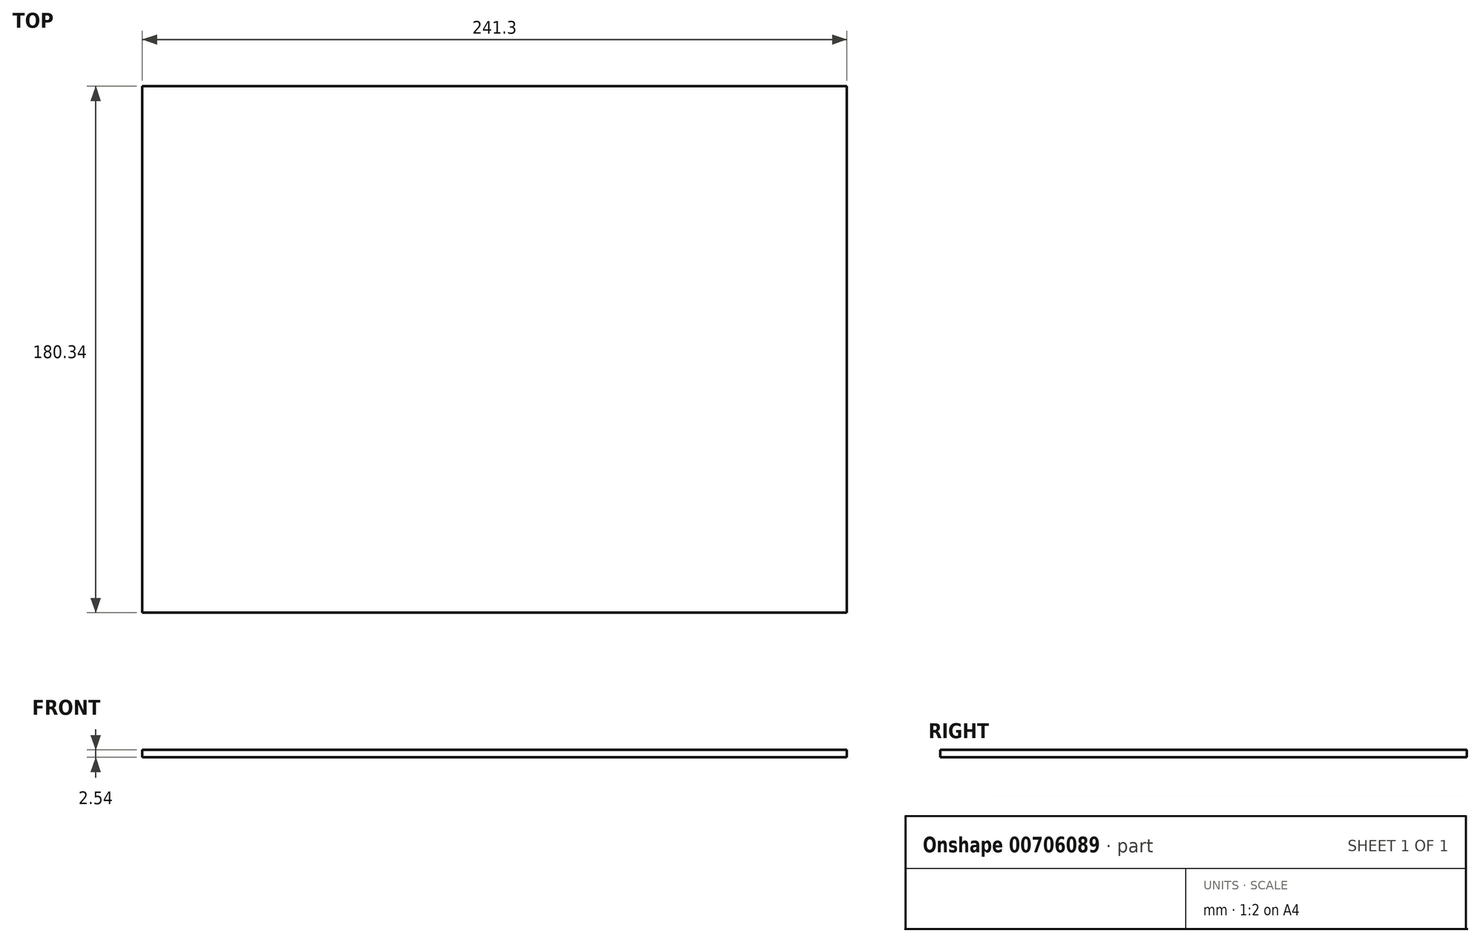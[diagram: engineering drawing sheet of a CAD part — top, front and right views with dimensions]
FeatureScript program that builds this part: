
annotation { "Feature Type Name" : "Feature", "Feature Type Description" : "" }
export const myFeature = defineFeature(function(context is Context, id is Id, definition is map)
    precondition{}
    {
        {
            var Q0;
            Q0=qCreatedBy(makeId("Top.planeOp"),FACE);
            var sketch = newSketch(context, id + "F0", { "sketchPlane" : qUnion([Q0])});
            skLineSegment(sketch, "E0.bottom", {"start": v(-120.65, -90.17) * mm, "end": v(120.65, -90.17) * mm});
            skLineSegment(sketch, "E0.top", {"start": v(-120.65, 90.17) * mm, "end": v(120.65, 90.17) * mm});
            skLineSegment(sketch, "E0.left", {"start": v(-120.65, -90.17) * mm, "end": v(-120.65, 90.17) * mm});
            skLineSegment(sketch, "E0.right", {"start": v(120.65, -90.17) * mm, "end": v(120.65, 90.17) * mm});
            skPoint(sketch, "E0.middle", {"position": v(0, 0) * mm});
            skSolve(sketch);
        }
        {
            var Q0;
            Q0 = qSketchRegion(id + "F0", true);
            extrude(context, id + "F1", {"entities" : qUnion([Q0]), "depth" : 2.54 * mm, "offsetDistance" : 25.4 * mm});
        }
    });
